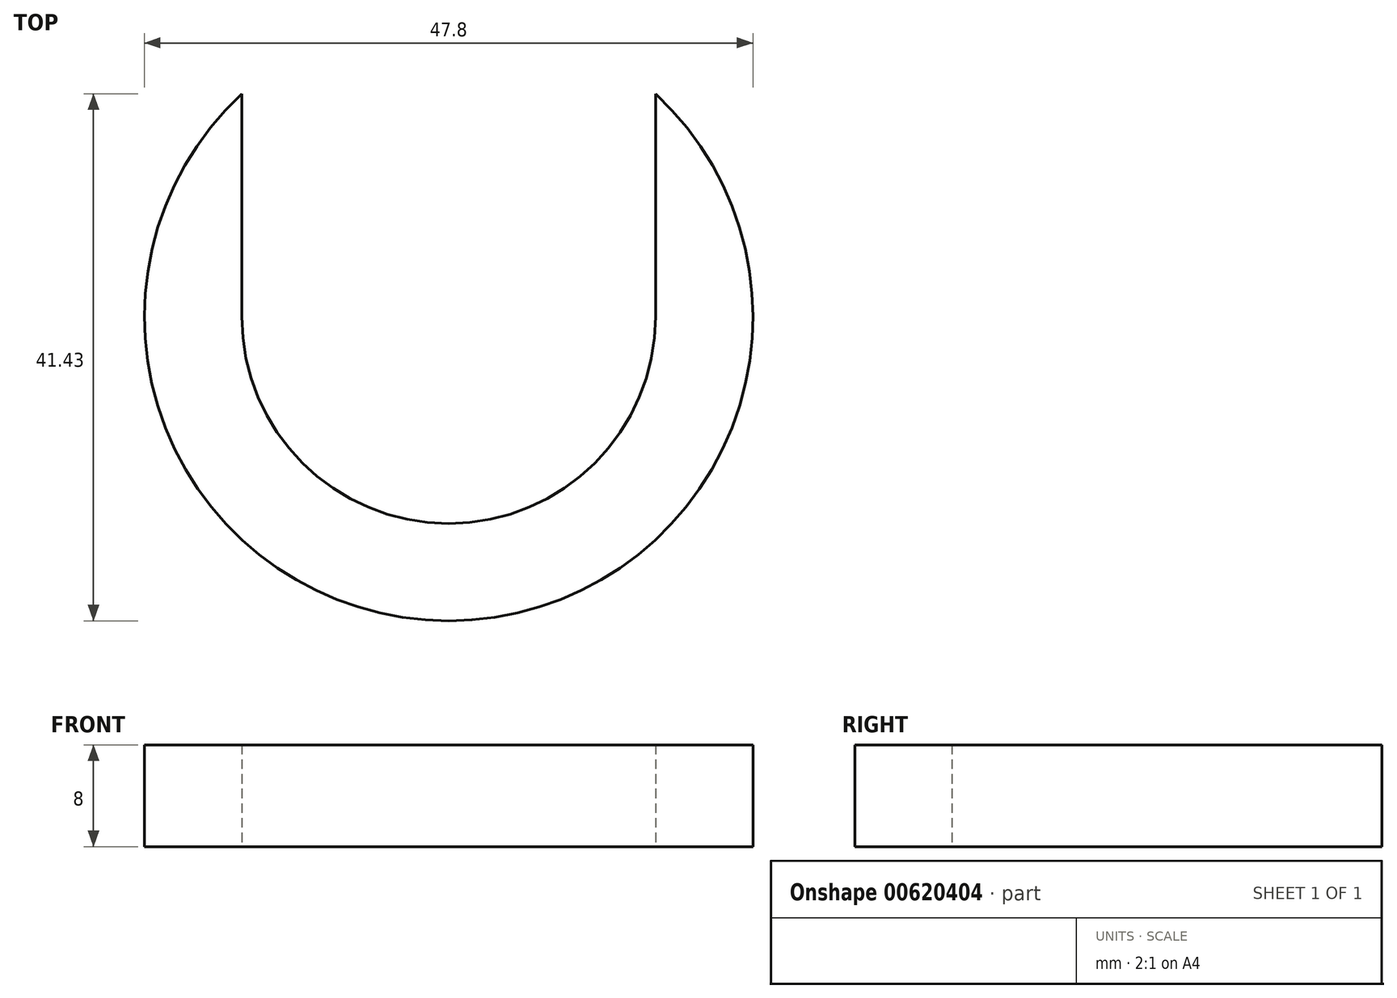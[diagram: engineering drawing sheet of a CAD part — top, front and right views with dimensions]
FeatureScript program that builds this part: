
annotation { "Feature Type Name" : "Feature", "Feature Type Description" : "" }
export const myFeature = defineFeature(function(context is Context, id is Id, definition is map)
    precondition{}
    {
        {
            var Q0;
            Q0=qCreatedBy(makeId("Top.planeOp"),FACE);
            var sketch = newSketch(context, id + "F0", { "sketchPlane" : qUnion([Q0])});
            skArc(sketch, "E0", {"start": v(-16.25, 17.53) * mm, "mid": v(0, -23.9) * mm, "end": v(16.25, 17.53) * mm});
            skArc(sketch, "E1", {"start": v(-16.25, 0) * mm, "mid": v(0, -16.25) * mm, "end": v(16.25, 0) * mm});
            skLineSegment(sketch, "E2", {"start": v(16.25, 0) * mm, "end": v(16.25, 17.53) * mm});
            skLineSegment(sketch, "E3", {"start": v(-16.25, 17.53) * mm, "end": v(-16.25, 0) * mm});
            skPoint(sketch, "E4.orphan", {"position": v(-16.25, 38.96) * mm});
            skSolve(sketch);
        }
        {
            var Q0;
            Q0=makeQuery(id+"F0.imprint","IMPRINT",FACE,{"disambiguationData":[TD([[makeQuery(id+"F0.imprint","IMPRINT",EDGE,{"derivedFrom":sQuery(id+"F0.wireOp",EDGE,"E0")}),1.0]])]});
            extrude(context, id + "F1", {"entities" : qUnion([Q0]), "depth" : 8 * mm, "offsetDistance" : 25 * mm});
        }
    });
